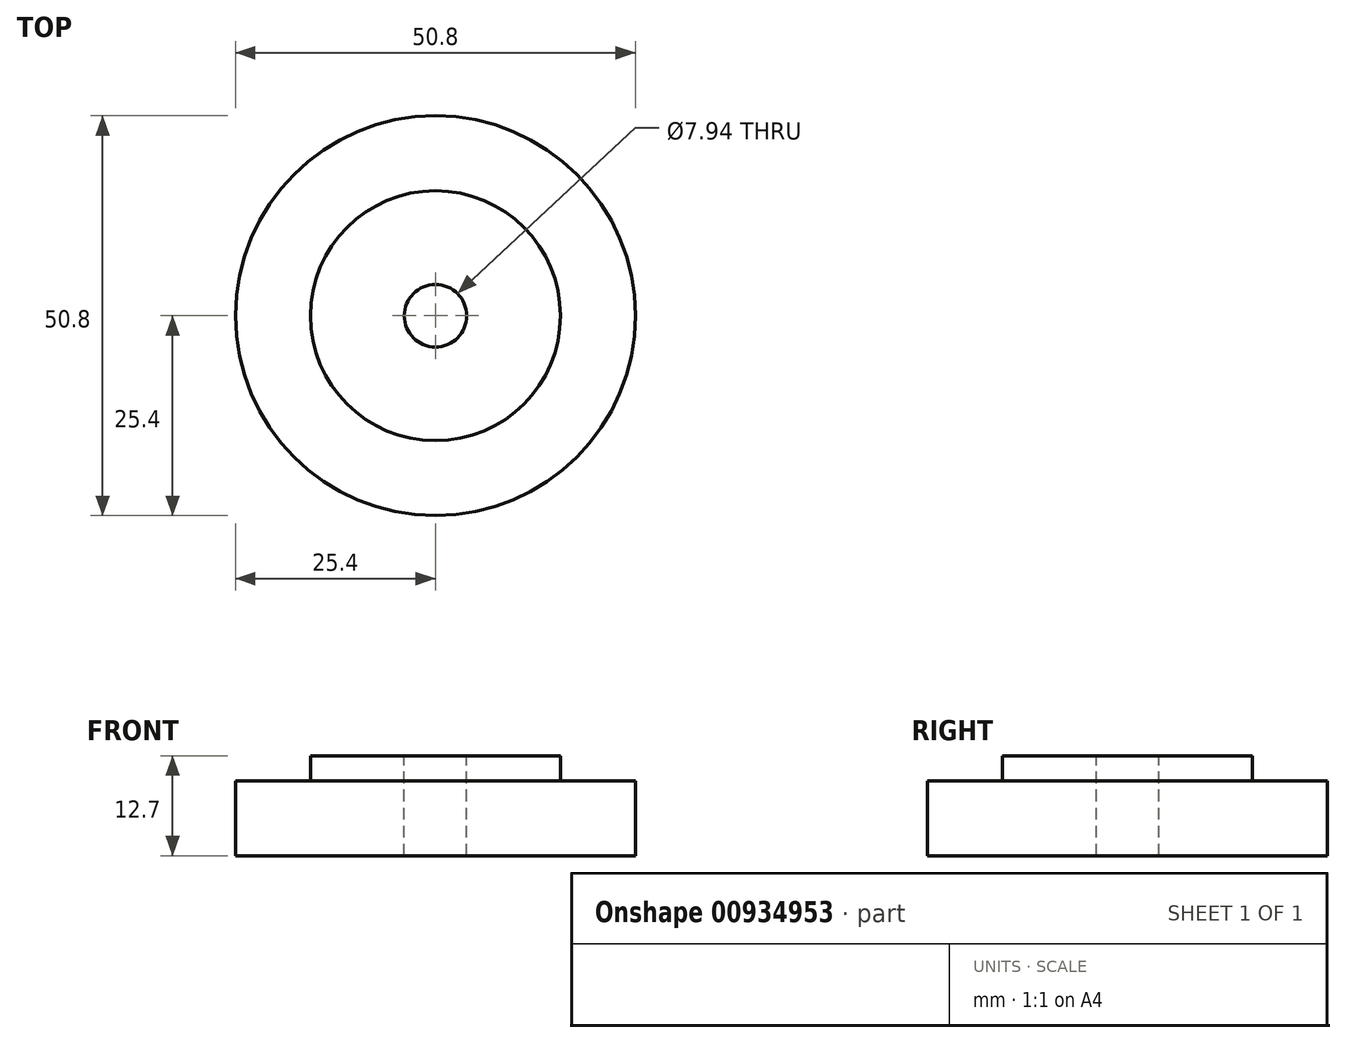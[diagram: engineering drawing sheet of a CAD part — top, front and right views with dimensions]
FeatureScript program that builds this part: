
annotation { "Feature Type Name" : "Feature", "Feature Type Description" : "" }
export const myFeature = defineFeature(function(context is Context, id is Id, definition is map)
    precondition{}
    {
        {
            var Q0;
            Q0=qCreatedBy(makeId("Top.planeOp"),FACE);
            var sketch = newSketch(context, id + "F0", { "sketchPlane" : qUnion([Q0])});
            skCircle(sketch, "E0", {"center": v(0, 0) * mm, "radius": 25.4 * mm});
            skSolve(sketch);
        }
        {
            var Q0;
            Q0=makeQuery(id+"F0.imprint","IMPRINT",FACE,{"disambiguationData":[TD([[makeQuery(id+"F0.imprint","IMPRINT",EDGE,{"derivedFrom":sQuery(id+"F0.wireOp",EDGE,"E0")}),1.0]])]});
            extrude(context, id + "F1", {"entities" : qUnion([Q0]), "depth" : 9.52 * mm, "offsetDistance" : 25.4 * mm});
        }
        {
            var Q0;
            Q0=makeQuery(id+"F1.opExtrude","CAP_FACE",FACE,{"disambiguationData":[OSD([sQuery(id+"F0.wireOp",EDGE,"E0")])],"isStart":false});
            var sketch = newSketch(context, id + "F2", { "sketchPlane" : qUnion([Q0])});
            skCircle(sketch, "E1", {"center": v(0, 0) * mm, "radius": 15.88 * mm});
            skSolve(sketch);
        }
        {
            var Q0;
            Q0=makeQuery(id+"F2.imprint","IMPRINT",FACE,{"disambiguationData":[TD([[makeQuery(id+"F2.imprint","IMPRINT",EDGE,{"derivedFrom":sQuery(id+"F2.wireOp",EDGE,"E1")}),1.0]])]});
            extrude(context, id + "F3", {"entities" : qUnion([Q0]), "operationType" : NewBodyOperationType.ADD, "depth" : 3.17 * mm, "offsetDistance" : 25.4 * mm});
        }
        {
            var Q0;
            Q0=makeQuery(id+"F3.opExtrude","CAP_FACE",FACE,{"disambiguationData":[OSD([sQuery(id+"F2.wireOp",EDGE,"E1")])],"isStart":false});
            var sketch = newSketch(context, id + "F4", { "sketchPlane" : qUnion([Q0])});
            skCircle(sketch, "E2", {"center": v(0, 0) * mm, "radius": 3.97 * mm});
            skSolve(sketch);
        }
        {
            var Q0;
            Q0 = qSketchRegion(id + "F4", true);
            extrude(context, id + "F5", {"entities" : qUnion([Q0]), "operationType" : NewBodyOperationType.REMOVE, "endBound" : BoundingType.THROUGH_ALL, "oppositeDirection" : true, "depth" : 25.4 * mm, "offsetDistance" : 25.4 * mm});
        }
    });
